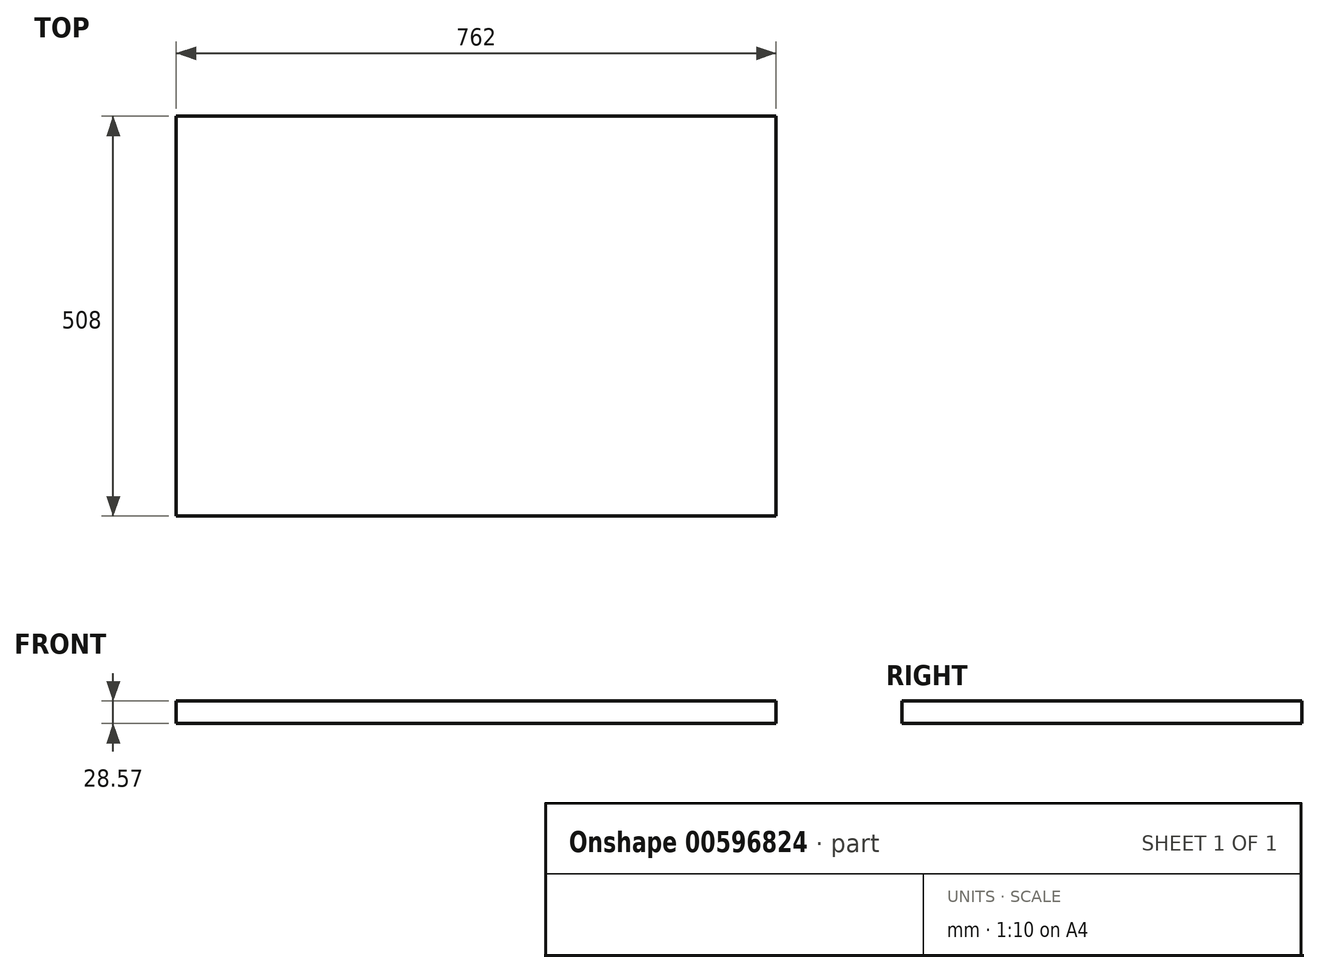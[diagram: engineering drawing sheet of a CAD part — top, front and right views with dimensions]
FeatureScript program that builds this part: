
annotation { "Feature Type Name" : "Feature", "Feature Type Description" : "" }
export const myFeature = defineFeature(function(context is Context, id is Id, definition is map)
    precondition{}
    {
        {
            var Q0;
            Q0=qCreatedBy(makeId("Top.planeOp"),FACE);
            var sketch = newSketch(context, id + "F0", { "sketchPlane" : qUnion([Q0])});
            skLineSegment(sketch, "E0.bottom", {"start": v(381, 254) * mm, "end": v(-381, 254) * mm});
            skLineSegment(sketch, "E0.top", {"start": v(381, -254) * mm, "end": v(-381, -254) * mm});
            skLineSegment(sketch, "E0.left", {"start": v(381, 254) * mm, "end": v(381, -254) * mm});
            skLineSegment(sketch, "E0.right", {"start": v(-381, 254) * mm, "end": v(-381, -254) * mm});
            skPoint(sketch, "E0.middle", {"position": v(0, 0) * mm});
            skSolve(sketch);
        }
        {
            var Q0;
            Q0=makeQuery(id+"F0.imprint","IMPRINT",FACE,{"disambiguationData":[TD([[makeQuery(id+"F0.imprint","IMPRINT",EDGE,{"derivedFrom":sQuery(id+"F0.wireOp",EDGE,"E0.bottom")}),1.0]])]});
            extrude(context, id + "F1", {"entities" : qUnion([Q0]), "depth" : 28.57 * mm, "offsetDistance" : 25.4 * mm});
        }
    });
